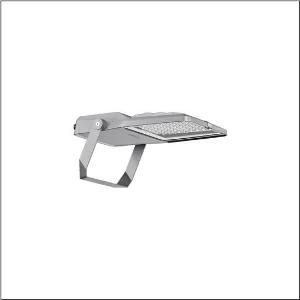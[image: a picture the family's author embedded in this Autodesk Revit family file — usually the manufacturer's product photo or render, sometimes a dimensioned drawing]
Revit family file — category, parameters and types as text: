
# Revit family: floodlight_fl_21_iq_mini___pl64_5xa7772d3e1a_da13
name_source: partatom
category: Lighting Fixtures
units: mm (PartAtom-declared; Revit-internal decimal feet)

## family parameters
Cut with Voids When Loaded = No
Host = Face
Light Source = No
Part Type = Normal
Room Calculation Point = No
Round Connector Dimension = Use Diameter
Shared = No

## types (1)
- --- (1 x LED, 14810 lm, 143 W, 3000K)
    Apparent Load = 143 VA
    CIE Flux Codes = 28 80 98 100 100
    Color Rendering = 80
    Color Temperature = 3000K
    Default Elevation = 1800 mm
    Description = Floodlight FL 21 iQ mini, floodlight, primary light control with lens, of PMMA, primary optical cover: protective disc, of toughened safety glass, transparent, light distribution: PL64, light emission: direct distribution, installation type: surface-mounted, lamps: LED, High Power LED, rated values: 14.810lm | 143W | 103,6lm/W (begin service life); end service life: 14.810lm | 151,6W; at 50% lumin. flux: 7.405lm | 60,5W | 122,4lm/W, colour temperature: 3000K, colour rendering: CRI > 80, light colour: 830, light setting 1 begin service life: 100% | 14.810lm | 143W | 103,6lm/W | 3.000K, light setting 1 end service life: 151,6W, further light settings possible, control: Street-Remote, Auto-Match, Temp-Guard, Night-Set, Smart-Wire, Desk-Remote (wireless, voltage-free reading and setting of iQ features in the workshop via application-optimized NFC function/RFID function), optimised constant luminous flux control (CLO 2.0), pre-setting: linear dimming characteristic, with terminal, 6-pole, mains connection: 220..240V, AC, 50/60Hz, luminaire housing, of diecast aluminium, powder-coated, SITECO metallic grey (DB 702S), corrosivity category C5 mid according to DIN EN ISO 12944suitable for swimming poolschlorine-resistant, sealing non-destructively replaceable, mounting bracket, of steel, galvanised, powder-coated, SITECO metallic grey (DB 702S), protection rating (complete): IP66, insulation class (complete): insulation class II (safety insulation), certification: CE, ENEC, VDE, protection symbol: D, impact resistance: IK08, permissible operating ambient temperature: -40..+40°C, permissible operating ambient temperature for outdoor applications: -40..+50°C, standard: DIN EN 12944, LABS conformity tested according to VDMA 24364:2018-05, packaging unit: 1 piece

Light Distribution: PL64
    Height = 70 mm
    Lamp = 1 x LED
    Lamp Light Flux = 14810 lm
    Lamp Power = 143 W
    Lamp count = 1
    Length = 485 mm
    Luminous efficacy = 104 lm/W
    Manufacturer = Siteco
    ModVariant = No
    Model = 5XA7772D3E1A
    Mounting Place = Pole
    Mounting Type = Pole annexe
    Number of Poles = 1
    OnlyDefault = Yes
    Power Factor = 1
    Product Name = Floodlight FL 21 iQ mini | PL64
    Product group = floodlight | pylon annexe
    ProductGroupID = 6201
    Protection Class = Protection class II
    Protection Degree = IP 66
    RLX_Detail_Level = 1
    RLX_Emergency_Light_Flux = 0 lm
    RLX_Emergency_Type = 0
    RLX_Emergency_Type_DB = No
    RlxData = <blob elided: 96621 chars, md5=1ae33923>
    Socket = socket
    Standby Power = 0 W
    System Light Flux = 14810 lm
    System Power = 143 W
    Type Comments = factory setting: luminous flux: 100 % | dim-lin: 254 | 730 mA
    Type Image = l_1006845.jpg
    URL = http://relux.com
    VarID = @adj_166797
    Voltage = 0 V
    Weight = 0.00 kg
    Width = 337 mm

## geometry (parser evidence)
native form markers: Blend x4, Sweep x11
no freeform markers — native parametric forms only
